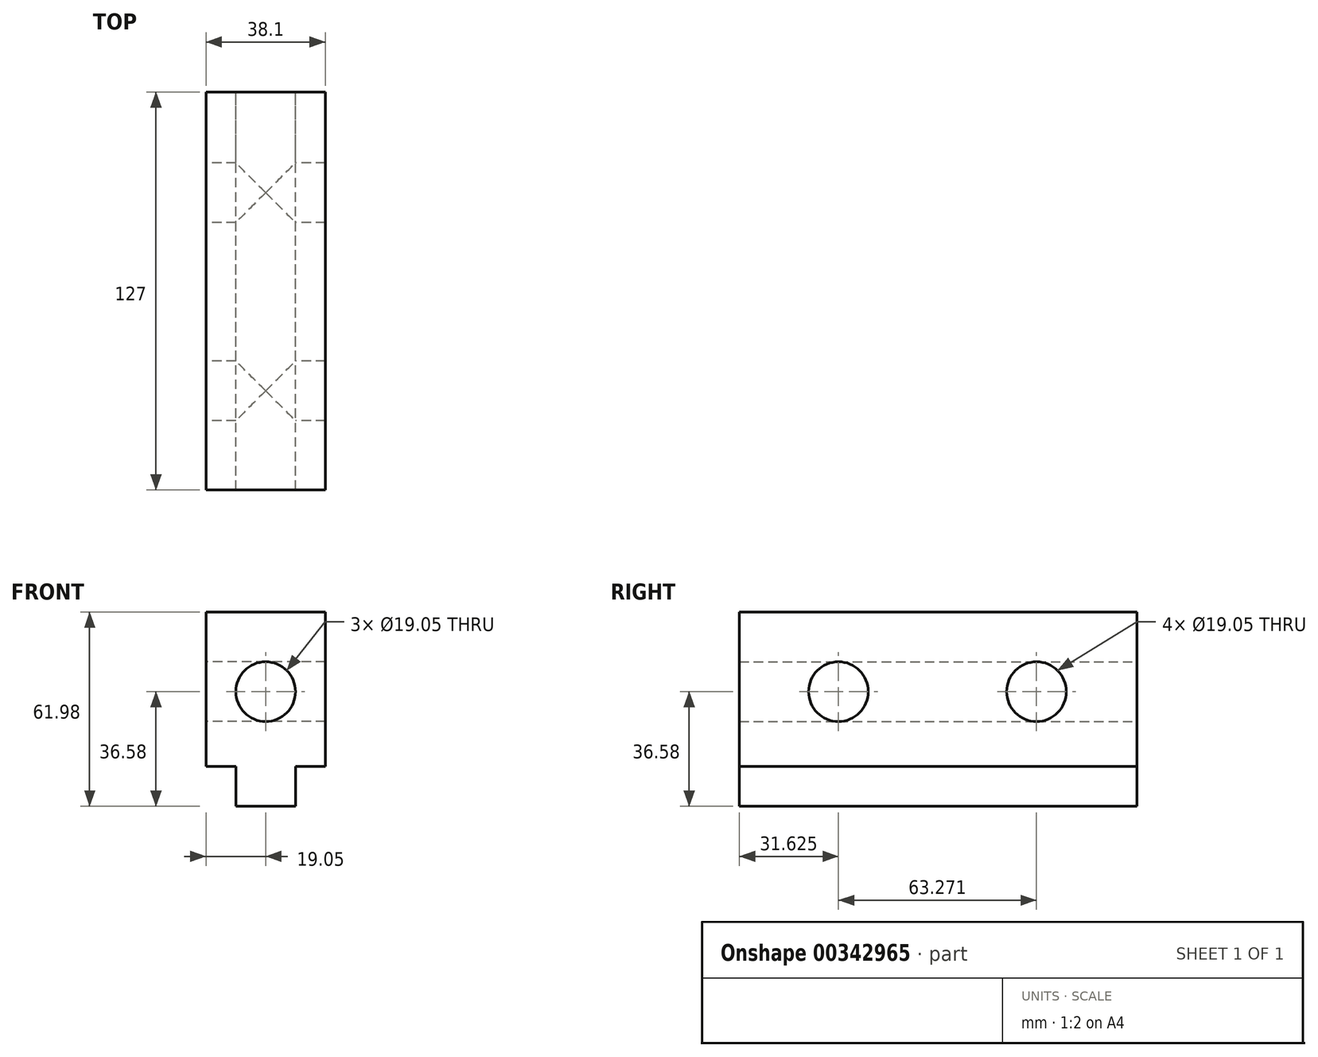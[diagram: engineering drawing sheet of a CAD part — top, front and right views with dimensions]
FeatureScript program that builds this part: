
annotation { "Feature Type Name" : "Feature", "Feature Type Description" : "" }
export const myFeature = defineFeature(function(context is Context, id is Id, definition is map)
    precondition{}
    {
        {
            var Q0;
            Q0=qCreatedBy(makeId("Front.planeOp"),FACE);
            var sketch = newSketch(context, id + "F0", { "sketchPlane" : qUnion([Q0])});
            skLineSegment(sketch, "E0", {"start": v(-9.52, -36.58) * mm, "end": v(9.52, -36.58) * mm});
            skLineSegment(sketch, "E1", {"start": v(9.53, -36.58) * mm, "end": v(9.53, -23.88) * mm});
            skLineSegment(sketch, "E2", {"start": v(-9.52, -36.58) * mm, "end": v(-9.52, -23.88) * mm});
            skLineSegment(sketch, "E3", {"start": v(-9.52, -23.88) * mm, "end": v(-19.05, -23.88) * mm});
            skLineSegment(sketch, "E4", {"start": v(9.53, -23.88) * mm, "end": v(19.05, -23.88) * mm});
            skLineSegment(sketch, "E5", {"start": v(-19.05, 25.4) * mm, "end": v(0, 25.4) * mm});
            skLineSegment(sketch, "E6", {"start": v(0, 25.4) * mm, "end": v(19.05, 25.4) * mm});
            skLineSegment(sketch, "E7", {"start": v(-19.05, -23.88) * mm, "end": v(-19.05, 0) * mm});
            skLineSegment(sketch, "E8", {"start": v(-19.05, 0) * mm, "end": v(-19.05, 25.4) * mm});
            skLineSegment(sketch, "E9", {"start": v(19.05, 25.4) * mm, "end": v(19.05, 0) * mm});
            skLineSegment(sketch, "E10", {"start": v(19.05, 0) * mm, "end": v(19.05, -23.88) * mm});
            skCircle(sketch, "E11", {"center": v(0, 0) * mm, "radius": 9.53 * mm});
            skSolve(sketch);
        }
        {
            var Q0;
            Q0 = qSketchRegion(id + "F0", true);
            extrude(context, id + "F1", {"entities" : qUnion([Q0]), "depth" : 127 * mm});
        }
        {
            var Q0;
            Q0=qCreatedBy(makeId("Right.planeOp"),FACE);
            var sketch = newSketch(context, id + "F2", { "sketchPlane" : qUnion([Q0])});
            skPoint(sketch, "E12.end.orphan", {"position": v(-30.84, 26.95) * mm});
            skPoint(sketch, "E13.end.orphan", {"position": v(0, 0) * mm});
            skPoint(sketch, "E13.start.orphan", {"position": v(0, 26.95) * mm});
            skPoint(sketch, "E14.end.orphan", {"position": v(-134, 0) * mm});
            skPoint(sketch, "E15.start.orphan", {"position": v(-134, 26.95) * mm});
            skLineSegment(sketch, "E16", {"start": v(0, 24.49) * mm, "end": v(-31.75, 24.49) * mm});
            skPoint(sketch, "E17.start.orphan", {"position": v(-127.12, 26.95) * mm});
            skLineSegment(sketch, "E18", {"start": v(-127.12, 26.95) * mm, "end": v(-95.37, 26.95) * mm});
            skCircle(sketch, "E19", {"center": v(-32.1, 0) * mm, "radius": 9.53 * mm});
            skCircle(sketch, "E20", {"center": v(-95.37, 0) * mm, "radius": 9.53 * mm});
            skSolve(sketch);
        }
        {
            var Q0;
            Q0 = qSketchRegion(id + "F2", true);
            extrude(context, id + "F3", {"entities" : qUnion([Q0]), "operationType" : NewBodyOperationType.REMOVE, "depth" : 38.1 * mm, "hasSecondDirection" : true, "secondDirectionOppositeDirection" : true, "secondDirectionDepth" : 38.1 * mm});
        }
    });
